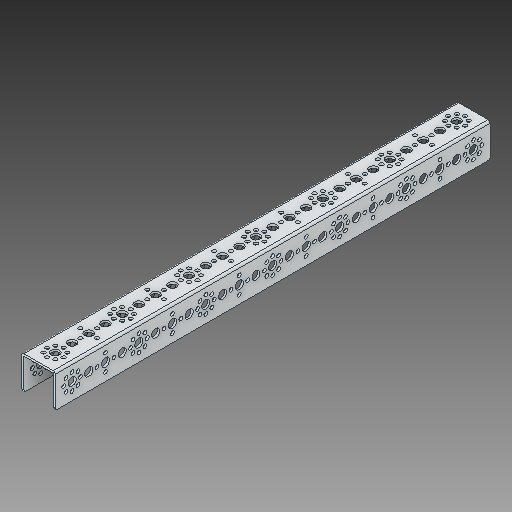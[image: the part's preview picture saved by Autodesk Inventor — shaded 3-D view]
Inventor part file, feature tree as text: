
AUTODESK INVENTOR PART (.ipt)
format: ipt  version: 2018 (Build 220112000, 112)  size: 478,208 bytes
history: native  units: in
note: dims shown in document units (in); Inventor stores cm internally (conversion verified against a paired STEP export)
features: fillet x1
ambient origin geometry x8: Origin, YZ Plane, XZ Plane, XY Plane, X Axis, Y Axis, Z Axis, Center Point
bodies: Solid1 (feature_tree)
feature tree (1):
  fillet  "Fillet1"  [1 undecoded]
note: 1 required parameter value undecoded (feature->parameter linkage not recoverable at this tier; creation-order binding heuristic only, values carry confidence <= 0.55)
